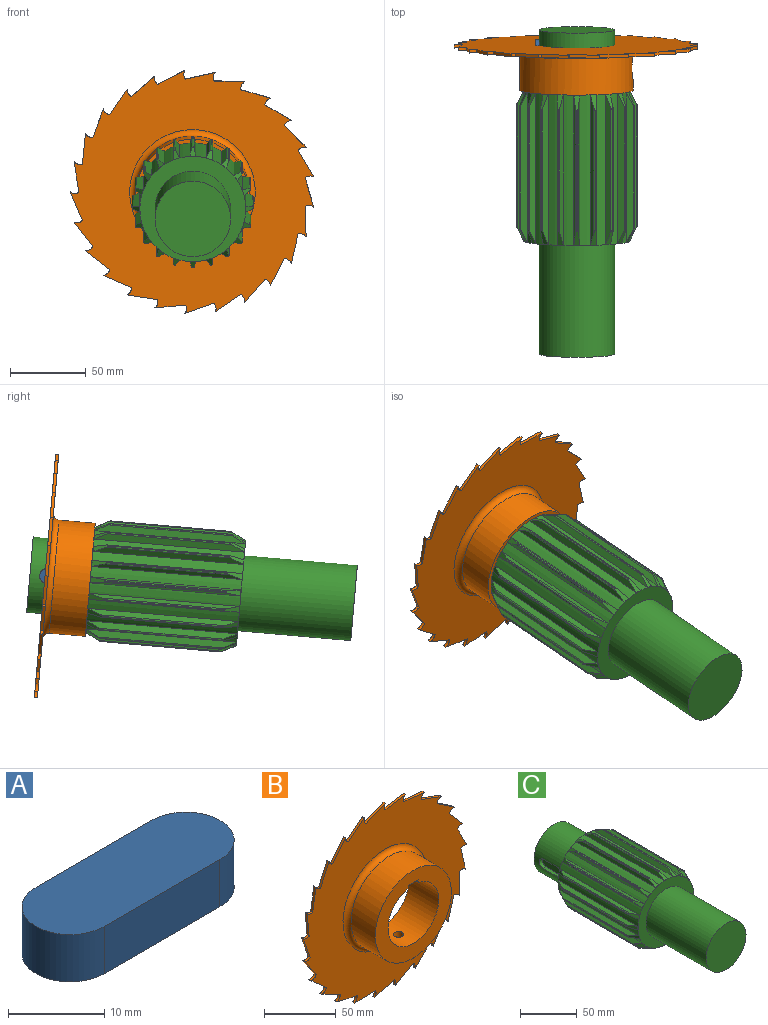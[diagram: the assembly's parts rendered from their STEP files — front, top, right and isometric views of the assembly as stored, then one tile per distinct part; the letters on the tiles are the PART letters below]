
ASSEMBLY  parts=3 mates=2
PART A: 6 faces, bbox 27x10x6 mm
  f0: plane 17x6mm, normal (0,1,0), area 102mm2, adj f1,f3,f4,f5
  f1: cylinder r=5mm len=10mm, axis (0,0,-1), area 94.2mm2, adj f0,f2,f4,f5
  f2: plane 17x6mm, normal (0,-1,0), area 102mm2, adj f1,f3,f4,f5
  f3: cylinder r=5mm len=10mm, axis (0,0,-1), area 94.2mm2, adj f0,f2,f4,f5
  f4: plane 27x10mm, normal (0,0,1), area 248.5mm2, adj f0,f1,f2,f3
  f5: plane 27x10mm, normal (0,0,-1), area 248.5mm2, adj f0,f1,f2,f3
PART B: 62 faces, bbox 161.2x30x160.9 mm
  f0: cylinder r=25mm len=50mm, axis (0,1,0), area 4371.8mm2, adj f6,f55,f56,f58,f61
  f1: cylinder r=37.5mm len=75mm, axis (0,1,0), area 5418.1mm2, adj f2,f58,f60
  f2: torus R=41.5mm, axis (0,-1,0), area 1537.7mm2, adj f1,f5,f59,f60
  f3: cylinder r=5mm len=4.13mm, axis (0,1,0), area 12.1mm2, adj f4,f5,f6,f54
  f4: plane 19.15x6.92mm, normal (0.34,0,0.94), area 40.7mm2, adj f3,f5,f6,f7
  f5: plane 161.18x160.86mm, normal (0,-1,0), area 13341.1mm2, adj f2,f3,f4,f7,f8,f9,f10,f11
  f6: plane 161.18x160.86mm, normal (0,1,0), area 16766.6mm2, adj f0,f3,f4,f7,f8,f9,f10,f11
  f7: cylinder r=5mm len=4.98mm, axis (0,1,0), area 12.1mm2, adj f4,f5,f6,f8
  f8: plane 20.27x2mm, normal (0.1,0,1), area 40.7mm2, adj f5,f6,f7,f9
  f9: cylinder r=5mm len=5.51mm, axis (0,1,0), area 12.1mm2, adj f5,f6,f8,f10
  f10: plane 20.12x3.16mm, normal (-0.16,0,0.99), area 40.7mm2, adj f5,f6,f9,f11
  f11: cylinder r=5mm len=5.7mm, axis (0,1,0), area 12.1mm2, adj f5,f6,f10,f12
  f12: plane 18.7x8.07mm, normal (-0.4,0,0.92), area 40.7mm2, adj f5,f6,f11,f13
  f13: cylinder r=5mm len=5.53mm, axis (0,1,0), area 12.1mm2, adj f5,f6,f12,f14
  f14: plane 16.1x12.46mm, normal (-0.61,0,0.79), area 40.7mm2, adj f5,f6,f13,f15
  f15: cylinder r=5mm len=5.01mm, axis (0,1,0), area 12.1mm2, adj f5,f6,f14,f16
  f16: plane 16.08x12.5mm, normal (-0.79,0,0.61), area 40.7mm2, adj f5,f6,f15,f17
  f17: cylinder r=5mm len=4.18mm, axis (0,1,0), area 12.1mm2, adj f5,f6,f16,f18
  f18: plane 18.68x8.11mm, normal (-0.92,0,0.4), area 40.7mm2, adj f5,f6,f17,f19
  f19: cylinder r=5mm len=4.79mm, axis (0,1,0), area 12.1mm2, adj f5,f6,f18,f20
  f20: plane 20.11x3.21mm, normal (-0.99,0,0.16), area 40.7mm2, adj f5,f6,f19,f21
  f21: cylinder r=5mm len=5.41mm, axis (0,1,0), area 12.1mm2, adj f5,f6,f20,f22
  f22: plane 20.28x2mm, normal (-1,0,-0.09), area 40.7mm2, adj f5,f6,f21,f23
  f23: cylinder r=5mm len=5.69mm, axis (0,1,0), area 12.1mm2, adj f5,f6,f22,f24
  f24: plane 19.17x6.88mm, normal (-0.94,0,-0.34), area 40.7mm2, adj f5,f6,f23,f25
  f25: cylinder r=5mm len=5.61mm, axis (0,1,0), area 12.1mm2, adj f5,f6,f24,f26
  f26: plane 16.86x11.43mm, normal (-0.83,0,-0.56), area 40.7mm2, adj f5,f6,f25,f27
  f27: cylinder r=5mm len=5.17mm, axis (0,1,0), area 12.1mm2, adj f5,f6,f26,f28
  f28: plane 15.26x13.48mm, normal (-0.66,0,-0.75), area 40.7mm2, adj f5,f6,f27,f29
  f29: cylinder r=5mm len=4.41mm, axis (0,1,0), area 12.1mm2, adj f5,f6,f28,f30
  f30: plane 18.13x9.27mm, normal (-0.45,0,-0.89), area 40.7mm2, adj f5,f6,f29,f31
  f31: cylinder r=5mm len=4.59mm, axis (0,1,0), area 12.1mm2, adj f5,f6,f30,f32
  f32: plane 19.87x4.46mm, normal (-0.22,0,-0.98), area 40.7mm2, adj f5,f6,f31,f33
  f33: cylinder r=5mm len=5.29mm, axis (0,1,0), area 12.1mm2, adj f5,f6,f32,f34
  f34: plane 20.35x2mm, normal (0.03,0,-1), area 40.7mm2, adj f5,f6,f33,f35
  f35: cylinder r=5mm len=5.65mm, axis (0,1,0), area 12.1mm2, adj f5,f6,f34,f36
  f36: plane 19.56x5.66mm, normal (0.28,0,-0.96), area 40.7mm2, adj f5,f6,f35,f37
  f37: cylinder r=5mm len=5.66mm, axis (0,1,0), area 12.1mm2, adj f5,f6,f36,f38
  f38: plane 17.54x10.35mm, normal (0.51,0,-0.86), area 40.7mm2, adj f5,f6,f37,f39
  f39: cylinder r=5mm len=5.31mm, axis (0,1,0), area 12.1mm2, adj f5,f6,f38,f40
  f40: plane 14.42x14.38mm, normal (0.71,0,-0.71), area 40.7mm2, adj f5,f6,f39,f41
  f41: cylinder r=5mm len=4.63mm, axis (0,1,0), area 12.1mm2, adj f5,f6,f40,f42
  f42: plane 17.52x10.39mm, normal (0.86,0,-0.51), area 40.7mm2, adj f5,f6,f41,f43
  f43: cylinder r=5mm len=4.37mm, axis (0,1,0), area 12.1mm2, adj f5,f6,f42,f44
  f44: plane 19.55x5.7mm, normal (0.96,0,-0.28), area 40.7mm2, adj f5,f6,f43,f45
  f45: cylinder r=5mm len=5.14mm, axis (0,1,0), area 12.1mm2, adj f5,f6,f44,f46
  f46: plane 20.35x2mm, normal (1,0,-0.03), area 40.7mm2, adj f5,f6,f45,f47
  f47: cylinder r=5mm len=5.59mm, axis (0,1,0), area 12.1mm2, adj f5,f6,f46,f48
  f48: plane 19.88x4.42mm, normal (0.98,0,0.22), area 40.7mm2, adj f5,f6,f47,f49
  f49: cylinder r=5mm len=5.69mm, axis (0,1,0), area 12.1mm2, adj f5,f6,f48,f50
  f50: plane 18.15x9.22mm, normal (0.89,0,0.45), area 40.7mm2, adj f5,f6,f49,f51
  f51: cylinder r=5mm len=5.43mm, axis (0,1,0), area 12.1mm2, adj f5,f6,f50,f52
  f52: plane 15.29x13.45mm, normal (0.75,0,0.66), area 40.7mm2, adj f5,f6,f51,f53
  f53: cylinder r=5mm len=4.83mm, axis (0,1,0), area 12.1mm2, adj f5,f6,f52,f54
  f54: plane 16.83x11.47mm, normal (0.56,0,0.83), area 40.7mm2, adj f3,f5,f6,f53
  f55: plane 30x2.51mm, normal (-1,0,0), area 75.2mm2, adj f0,f6,f57,f58
  f56: plane 30x2.51mm, normal (1,0,0), area 75.2mm2, adj f0,f6,f57,f58
  f57: plane 30x10mm, normal (0,0,-1), area 300mm2, adj f6,f55,f56,f58
  f58: plane 75x75mm, normal (0,-1,0), area 2432.7mm2, adj f0,f1,f55,f56,f57
  f59: plane 0.72x0.13mm, normal (0,0,1), area 0mm2, adj f2,f60
  f60: cone r=3.5mm half-angle=45deg, axis (0,0,-1), area 278.3mm2, adj f1,f2,f59,f61
  f61: cylinder r=3.5mm len=7.12mm, axis (0,0,-1), area 153.9mm2, adj f0,f60
PART C: 194 faces, bbox 80.1x215.1x80.1 mm
  f0: cylinder r=25mm len=50mm, axis (0,1,0), area 5994.6mm2, adj f1,f4,f187,f188,f189,f190,f192
  f1: plane 50x50mm, normal (0,1,0), area 1963.5mm2, adj f0
  f2: cylinder r=35mm len=100mm, axis (0,1,0), area 14010.6mm2, adj f3,f4,f5,f6,f8,f9,f14,f15
  f3: plane 70x70mm, normal (0,-1,0), area 1885mm2, adj f2,f185
  f4: plane 70x70mm, normal (0,1,0), area 1885mm2, adj f0,f2
  f5: plane 99.85x4.49mm, normal (0.97,0,0.24), area 420.8mm2, adj f2,f8,f9,f12
  f6: plane 99.85x4.49mm, normal (-0.97,0,0.24), area 420.8mm2, adj f2,f8,f9,f11
  f7: plane 79.64x0.33mm, normal (0,0,1), area 25.9mm2, adj f10,f11,f12,f13
  f8: plane 9.77x4.98mm, normal (0,-0.45,0.89), area 29.9mm2, adj f2,f5,f6,f11,f12,f13
  f9: plane 9.77x4.98mm, normal (0,0.45,0.89), area 29.9mm2, adj f2,f5,f6,f10,f11,f12
  f10: cylinder r=0.75mm len=1.01mm, axis (1,0,0), area 0.2mm2, adj f7,f9,f11,f12
  f11: cylinder r=0.75mm len=82.24mm, axis (0,1,0), area 80.5mm2, adj f6,f7,f8,f9,f10,f13
  f12: cylinder r=0.75mm len=82.24mm, axis (0,1,0), area 80.5mm2, adj f5,f7,f8,f9,f10,f13
  f13: cylinder r=0.75mm len=1.01mm, axis (1,0,0), area 0.2mm2, adj f7,f8,f11,f12
  f14: plane 99.85x3.93mm, normal (0.85,0,0.53), area 420.8mm2, adj f2,f17,f18,f21
  f15: plane 99.85x4.61mm, normal (-1,0,-0.07), area 420.8mm2, adj f2,f17,f18,f20
  f16: plane 79.64x0.31mm, normal (-0.31,0,0.95), area 25.9mm2, adj f19,f20,f21,f22
  f17: plane 9.77x5.51mm, normal (-0.28,-0.45,0.85), area 29.9mm2, adj f2,f14,f15,f20,f21,f22
  f18: plane 9.77x5.51mm, normal (-0.28,0.45,0.85), area 29.9mm2, adj f2,f14,f15,f19,f20,f21
  f19: cylinder r=0.75mm len=0.98mm, axis (0.95,0,0.31), area 0.2mm2, adj f16,f18,f20,f21
  f20: cylinder r=0.75mm len=82.24mm, axis (0,1,0), area 80.5mm2, adj f15,f16,f17,f18,f19,f22
  f21: cylinder r=0.75mm len=82.24mm, axis (0,1,0), area 80.5mm2, adj f14,f16,f17,f18,f19,f22
  f22: cylinder r=0.75mm len=0.98mm, axis (0.95,0,0.31), area 0.2mm2, adj f16,f17,f20,f21
  f23: plane 99.85x3.53mm, normal (0.64,0,0.76), area 420.8mm2, adj f2,f26,f27,f30
  f24: plane 99.85x4.28mm, normal (-0.93,0,-0.38), area 420.8mm2, adj f2,f26,f27,f29
  f25: plane 79.64x0.26mm, normal (-0.59,0,0.81), area 25.9mm2, adj f28,f29,f30,f31
  f26: plane 9.77x5.51mm, normal (-0.52,-0.45,0.72), area 29.9mm2, adj f2,f23,f24,f29,f30,f31
  f27: plane 9.77x5.51mm, normal (-0.52,0.45,0.72), area 29.9mm2, adj f2,f23,f24,f28,f29,f30
  f28: cylinder r=0.75mm len=0.86mm, axis (0.81,0,0.59), area 0.2mm2, adj f25,f27,f29,f30
  f29: cylinder r=0.75mm len=82.24mm, axis (0,1,0), area 80.5mm2, adj f24,f25,f26,f27,f28,f31
  f30: cylinder r=0.75mm len=82.24mm, axis (0,1,0), area 80.5mm2, adj f23,f25,f26,f27,f28,f31
  f31: cylinder r=0.75mm len=0.86mm, axis (0.81,0,0.59), area 0.2mm2, adj f25,f26,f29,f30
  f32: plane 99.85x4.28mm, normal (0.38,0,0.93), area 420.8mm2, adj f2,f35,f36,f39
  f33: plane 99.85x3.53mm, normal (-0.76,0,-0.64), area 420.8mm2, adj f2,f35,f36,f38
  f34: plane 79.64x0.26mm, normal (-0.81,0,0.59), area 25.9mm2, adj f37,f38,f39,f40
  f35: plane 9.77x5.51mm, normal (-0.72,-0.45,0.52), area 29.9mm2, adj f2,f32,f33,f38,f39,f40
  f36: plane 9.77x5.51mm, normal (-0.72,0.45,0.52), area 29.9mm2, adj f2,f32,f33,f37,f38,f39
  f37: cylinder r=0.75mm len=0.86mm, axis (0.59,0,0.81), area 0.2mm2, adj f34,f36,f38,f39
  f38: cylinder r=0.75mm len=82.24mm, axis (0,1,0), area 80.5mm2, adj f33,f34,f35,f36,f37,f40
  f39: cylinder r=0.75mm len=82.24mm, axis (0,1,0), area 80.5mm2, adj f32,f34,f35,f36,f37,f40
  f40: cylinder r=0.75mm len=0.86mm, axis (0.59,0,0.81), area 0.2mm2, adj f34,f35,f38,f39
  f41: plane 99.85x4.61mm, normal (0.07,0,1), area 420.8mm2, adj f2,f44,f45,f48
  f42: plane 99.85x3.93mm, normal (-0.53,0,-0.85), area 420.8mm2, adj f2,f44,f45,f47
  f43: plane 79.64x0.31mm, normal (-0.95,0,0.31), area 25.9mm2, adj f46,f47,f48,f49
  f44: plane 9.77x5.51mm, normal (-0.85,-0.45,0.28), area 29.9mm2, adj f2,f41,f42,f47,f48,f49
  f45: plane 9.77x5.51mm, normal (-0.85,0.45,0.28), area 29.9mm2, adj f2,f41,f42,f46,f47,f48
  f46: cylinder r=0.75mm len=0.98mm, axis (0.31,0,0.95), area 0.2mm2, adj f43,f45,f47,f48
  f47: cylinder r=0.75mm len=82.24mm, axis (0,1,0), area 80.5mm2, adj f42,f43,f44,f45,f46,f49
  f48: cylinder r=0.75mm len=82.24mm, axis (0,1,0), area 80.5mm2, adj f41,f43,f44,f45,f46,f49
  f49: cylinder r=0.75mm len=0.98mm, axis (0.31,0,0.95), area 0.2mm2, adj f43,f44,f47,f48
  f50: plane 99.85x4.49mm, normal (-0.24,0,0.97), area 420.8mm2, adj f2,f53,f54,f57
  f51: plane 99.85x4.49mm, normal (-0.24,0,-0.97), area 420.8mm2, adj f2,f53,f54,f56
  f52: plane 79.64x0.33mm, normal (-1,0,0), area 25.9mm2, adj f55,f56,f57,f58
  f53: plane 9.77x4.98mm, normal (-0.89,-0.45,0), area 29.9mm2, adj f2,f50,f51,f56,f57,f58
  f54: plane 9.77x4.98mm, normal (-0.89,0.45,0), area 29.9mm2, adj f2,f50,f51,f55,f56,f57
  f55: cylinder r=0.75mm len=1.01mm, axis (0,0,1), area 0.2mm2, adj f52,f54,f56,f57
  f56: cylinder r=0.75mm len=82.24mm, axis (0,1,0), area 80.5mm2, adj f51,f52,f53,f54,f55,f58
  f57: cylinder r=0.75mm len=82.24mm, axis (0,1,0), area 80.5mm2, adj f50,f52,f53,f54,f55,f58
  f58: cylinder r=0.75mm len=1.01mm, axis (0,0,1), area 0.2mm2, adj f52,f53,f56,f57
  f59: plane 99.85x3.93mm, normal (-0.53,0,0.85), area 420.8mm2, adj f2,f62,f63,f66
  f60: plane 99.85x4.61mm, normal (0.07,0,-1), area 420.8mm2, adj f2,f62,f63,f65
  f61: plane 79.64x0.31mm, normal (-0.95,0,-0.31), area 25.9mm2, adj f64,f65,f66,f67
  f62: plane 9.77x5.51mm, normal (-0.85,-0.45,-0.28), area 29.9mm2, adj f2,f59,f60,f65,f66,f67
  f63: plane 9.77x5.51mm, normal (-0.85,0.45,-0.28), area 29.9mm2, adj f2,f59,f60,f64,f65,f66
  f64: cylinder r=0.75mm len=0.98mm, axis (-0.31,0,0.95), area 0.2mm2, adj f61,f63,f65,f66
  f65: cylinder r=0.75mm len=82.24mm, axis (0,1,0), area 80.5mm2, adj f60,f61,f62,f63,f64,f67
  f66: cylinder r=0.75mm len=82.24mm, axis (0,1,0), area 80.5mm2, adj f59,f61,f62,f63,f64,f67
  f67: cylinder r=0.75mm len=0.98mm, axis (-0.31,0,0.95), area 0.2mm2, adj f61,f62,f65,f66
  f68: plane 99.85x3.53mm, normal (-0.76,0,0.64), area 420.8mm2, adj f2,f71,f72,f75
  f69: plane 99.85x4.28mm, normal (0.38,0,-0.93), area 420.8mm2, adj f2,f71,f72,f74
  f70: plane 79.64x0.26mm, normal (-0.81,0,-0.59), area 25.9mm2, adj f73,f74,f75,f76
  f71: plane 9.77x5.51mm, normal (-0.72,-0.45,-0.52), area 29.9mm2, adj f2,f68,f69,f74,f75,f76
  f72: plane 9.77x5.51mm, normal (-0.72,0.45,-0.52), area 29.9mm2, adj f2,f68,f69,f73,f74,f75
  f73: cylinder r=0.75mm len=0.86mm, axis (-0.59,0,0.81), area 0.2mm2, adj f70,f72,f74,f75
  f74: cylinder r=0.75mm len=82.24mm, axis (0,1,0), area 80.5mm2, adj f69,f70,f71,f72,f73,f76
  f75: cylinder r=0.75mm len=82.24mm, axis (0,1,0), area 80.5mm2, adj f68,f70,f71,f72,f73,f76
  f76: cylinder r=0.75mm len=0.86mm, axis (-0.59,0,0.81), area 0.2mm2, adj f70,f71,f74,f75
  f77: plane 99.85x4.28mm, normal (-0.93,0,0.38), area 420.8mm2, adj f2,f80,f81,f84
  f78: plane 99.85x3.53mm, normal (0.64,0,-0.76), area 420.8mm2, adj f2,f80,f81,f83
  f79: plane 79.64x0.26mm, normal (-0.59,0,-0.81), area 25.9mm2, adj f82,f83,f84,f85
  f80: plane 9.77x5.51mm, normal (-0.52,-0.45,-0.72), area 29.9mm2, adj f2,f77,f78,f83,f84,f85
  f81: plane 9.77x5.51mm, normal (-0.52,0.45,-0.72), area 29.9mm2, adj f2,f77,f78,f82,f83,f84
  f82: cylinder r=0.75mm len=0.86mm, axis (-0.81,0,0.59), area 0.2mm2, adj f79,f81,f83,f84
  f83: cylinder r=0.75mm len=82.24mm, axis (0,1,0), area 80.5mm2, adj f78,f79,f80,f81,f82,f85
  f84: cylinder r=0.75mm len=82.24mm, axis (0,1,0), area 80.5mm2, adj f77,f79,f80,f81,f82,f85
  f85: cylinder r=0.75mm len=0.86mm, axis (-0.81,0,0.59), area 0.2mm2, adj f79,f80,f83,f84
  f86: plane 99.85x4.61mm, normal (-1,0,0.07), area 420.8mm2, adj f2,f89,f90,f93
  f87: plane 99.85x3.93mm, normal (0.85,0,-0.53), area 420.8mm2, adj f2,f89,f90,f92
  f88: plane 79.64x0.31mm, normal (-0.31,0,-0.95), area 25.9mm2, adj f91,f92,f93,f94
  f89: plane 9.77x5.51mm, normal (-0.28,-0.45,-0.85), area 29.9mm2, adj f2,f86,f87,f92,f93,f94
  f90: plane 9.77x5.51mm, normal (-0.28,0.45,-0.85), area 29.9mm2, adj f2,f86,f87,f91,f92,f93
  f91: cylinder r=0.75mm len=0.98mm, axis (-0.95,0,0.31), area 0.2mm2, adj f88,f90,f92,f93
  f92: cylinder r=0.75mm len=82.24mm, axis (0,1,0), area 80.5mm2, adj f87,f88,f89,f90,f91,f94
  f93: cylinder r=0.75mm len=82.24mm, axis (0,1,0), area 80.5mm2, adj f86,f88,f89,f90,f91,f94
  f94: cylinder r=0.75mm len=0.98mm, axis (-0.95,0,0.31), area 0.2mm2, adj f88,f89,f92,f93
  f95: plane 99.85x4.49mm, normal (-0.97,0,-0.24), area 420.8mm2, adj f2,f98,f99,f102
  f96: plane 99.85x4.49mm, normal (0.97,0,-0.24), area 420.8mm2, adj f2,f98,f99,f101
  f97: plane 79.64x0.33mm, normal (0,0,-1), area 25.9mm2, adj f100,f101,f102,f103
  f98: plane 9.82x5.03mm, normal (0,-0.45,-0.89), area 29.9mm2, adj f2,f95,f96,f101,f102,f103
  f99: plane 9.82x5.03mm, normal (0,0.45,-0.89), area 29.9mm2, adj f2,f95,f96,f100,f101,f102
  f100: cylinder r=0.75mm len=1.01mm, axis (-1,0,0), area 0.2mm2, adj f97,f99,f101,f102
  f101: cylinder r=0.75mm len=82.24mm, axis (0,1,0), area 80.5mm2, adj f96,f97,f98,f99,f100,f103
  f102: cylinder r=0.75mm len=82.24mm, axis (0,1,0), area 80.5mm2, adj f95,f97,f98,f99,f100,f103
  f103: cylinder r=0.75mm len=1.01mm, axis (-1,0,0), area 0.2mm2, adj f97,f98,f101,f102
  f104: plane 99.85x3.93mm, normal (-0.85,0,-0.53), area 420.8mm2, adj f2,f107,f108,f111
  f105: plane 99.85x4.61mm, normal (1,0,0.07), area 420.8mm2, adj f2,f107,f108,f110
  f106: plane 79.64x0.31mm, normal (0.31,0,-0.95), area 25.9mm2, adj f109,f110,f111,f112
  f107: plane 9.77x5.51mm, normal (0.28,-0.45,-0.85), area 29.9mm2, adj f2,f104,f105,f110,f111,f112
  f108: plane 9.77x5.51mm, normal (0.28,0.45,-0.85), area 29.9mm2, adj f2,f104,f105,f109,f110,f111
  f109: cylinder r=0.75mm len=0.98mm, axis (-0.95,0,-0.31), area 0.2mm2, adj f106,f108,f110,f111
  f110: cylinder r=0.75mm len=82.24mm, axis (0,1,0), area 80.5mm2, adj f105,f106,f107,f108,f109,f112
  f111: cylinder r=0.75mm len=82.24mm, axis (0,1,0), area 80.5mm2, adj f104,f106,f107,f108,f109,f112
  f112: cylinder r=0.75mm len=0.98mm, axis (-0.95,0,-0.31), area 0.2mm2, adj f106,f107,f110,f111
  f113: plane 99.85x3.53mm, normal (-0.64,0,-0.76), area 420.8mm2, adj f2,f116,f117,f120
  f114: plane 99.85x4.28mm, normal (0.93,0,0.38), area 420.8mm2, adj f2,f116,f117,f119
  f115: plane 79.64x0.26mm, normal (0.59,0,-0.81), area 25.9mm2, adj f118,f119,f120,f121
  f116: plane 9.77x5.51mm, normal (0.52,-0.45,-0.72), area 29.9mm2, adj f2,f113,f114,f119,f120,f121
  f117: plane 9.77x5.51mm, normal (0.52,0.45,-0.72), area 29.9mm2, adj f2,f113,f114,f118,f119,f120
  f118: cylinder r=0.75mm len=0.86mm, axis (-0.81,0,-0.59), area 0.2mm2, adj f115,f117,f119,f120
  f119: cylinder r=0.75mm len=82.24mm, axis (0,1,0), area 80.5mm2, adj f114,f115,f116,f117,f118,f121
  f120: cylinder r=0.75mm len=82.24mm, axis (0,1,0), area 80.5mm2, adj f113,f115,f116,f117,f118,f121
  f121: cylinder r=0.75mm len=0.86mm, axis (-0.81,0,-0.59), area 0.2mm2, adj f115,f116,f119,f120
  f122: plane 99.85x4.28mm, normal (-0.38,0,-0.93), area 420.8mm2, adj f2,f125,f126,f129
  f123: plane 99.85x3.53mm, normal (0.76,0,0.64), area 420.8mm2, adj f2,f125,f126,f128
  f124: plane 79.64x0.26mm, normal (0.81,0,-0.59), area 25.9mm2, adj f127,f128,f129,f130
  f125: plane 9.77x5.51mm, normal (0.72,-0.45,-0.52), area 29.9mm2, adj f2,f122,f123,f128,f129,f130
  f126: plane 9.77x5.51mm, normal (0.72,0.45,-0.52), area 29.9mm2, adj f2,f122,f123,f127,f128,f129
  f127: cylinder r=0.75mm len=0.86mm, axis (-0.59,0,-0.81), area 0.2mm2, adj f124,f126,f128,f129
  f128: cylinder r=0.75mm len=82.24mm, axis (0,1,0), area 80.5mm2, adj f123,f124,f125,f126,f127,f130
  f129: cylinder r=0.75mm len=82.24mm, axis (0,1,0), area 80.5mm2, adj f122,f124,f125,f126,f127,f130
  f130: cylinder r=0.75mm len=0.86mm, axis (-0.59,0,-0.81), area 0.2mm2, adj f124,f125,f128,f129
  f131: plane 99.85x4.61mm, normal (-0.07,0,-1), area 420.8mm2, adj f2,f134,f135,f138
  f132: plane 99.85x3.93mm, normal (0.53,0,0.85), area 420.8mm2, adj f2,f134,f135,f137
  f133: plane 79.64x0.31mm, normal (0.95,0,-0.31), area 25.9mm2, adj f136,f137,f138,f139
  f134: plane 9.77x5.51mm, normal (0.85,-0.45,-0.28), area 29.9mm2, adj f2,f131,f132,f137,f138,f139
  f135: plane 9.77x5.51mm, normal (0.85,0.45,-0.28), area 29.9mm2, adj f2,f131,f132,f136,f137,f138
  f136: cylinder r=0.75mm len=0.98mm, axis (-0.31,0,-0.95), area 0.2mm2, adj f133,f135,f137,f138
  f137: cylinder r=0.75mm len=82.24mm, axis (0,1,0), area 80.5mm2, adj f132,f133,f134,f135,f136,f139
  f138: cylinder r=0.75mm len=82.24mm, axis (0,1,0), area 80.5mm2, adj f131,f133,f134,f135,f136,f139
  f139: cylinder r=0.75mm len=0.98mm, axis (-0.31,0,-0.95), area 0.2mm2, adj f133,f134,f137,f138
  f140: plane 99.85x4.49mm, normal (0.24,0,-0.97), area 420.8mm2, adj f2,f143,f144,f147
  f141: plane 99.85x4.49mm, normal (0.24,0,0.97), area 420.8mm2, adj f2,f143,f144,f146
  f142: plane 79.64x0.33mm, normal (1,0,0), area 25.9mm2, adj f145,f146,f147,f148
  f143: plane 9.77x4.98mm, normal (0.89,-0.45,0), area 29.9mm2, adj f2,f140,f141,f146,f147,f148
  f144: plane 9.77x4.98mm, normal (0.89,0.45,0), area 29.9mm2, adj f2,f140,f141,f145,f146,f147
  f145: cylinder r=0.75mm len=1.01mm, axis (0,0,-1), area 0.2mm2, adj f142,f144,f146,f147
  f146: cylinder r=0.75mm len=82.24mm, axis (0,1,0), area 80.5mm2, adj f141,f142,f143,f144,f145,f148
  f147: cylinder r=0.75mm len=82.24mm, axis (0,1,0), area 80.5mm2, adj f140,f142,f143,f144,f145,f148
  f148: cylinder r=0.75mm len=1.01mm, axis (0,0,-1), area 0.2mm2, adj f142,f143,f146,f147
  f149: plane 99.85x3.93mm, normal (0.53,0,-0.85), area 420.8mm2, adj f2,f152,f153,f156
  f150: plane 99.85x4.61mm, normal (-0.07,0,1), area 420.8mm2, adj f2,f152,f153,f155
  f151: plane 79.64x0.31mm, normal (0.95,0,0.31), area 25.9mm2, adj f154,f155,f156,f157
  f152: plane 9.77x5.51mm, normal (0.85,-0.45,0.28), area 29.9mm2, adj f2,f149,f150,f155,f156,f157
  f153: plane 9.77x5.51mm, normal (0.85,0.45,0.28), area 29.9mm2, adj f2,f149,f150,f154,f155,f156
  f154: cylinder r=0.75mm len=0.98mm, axis (0.31,0,-0.95), area 0.2mm2, adj f151,f153,f155,f156
  f155: cylinder r=0.75mm len=82.24mm, axis (0,1,0), area 80.5mm2, adj f150,f151,f152,f153,f154,f157
  f156: cylinder r=0.75mm len=82.24mm, axis (0,1,0), area 80.5mm2, adj f149,f151,f152,f153,f154,f157
  f157: cylinder r=0.75mm len=0.98mm, axis (0.31,0,-0.95), area 0.2mm2, adj f151,f152,f155,f156
  f158: plane 99.85x3.53mm, normal (0.76,0,-0.64), area 420.8mm2, adj f2,f161,f162,f165
  f159: plane 99.85x4.28mm, normal (-0.38,0,0.93), area 420.8mm2, adj f2,f161,f162,f164
  f160: plane 79.64x0.26mm, normal (0.81,0,0.59), area 25.9mm2, adj f163,f164,f165,f166
  f161: plane 9.77x5.51mm, normal (0.72,-0.45,0.52), area 29.9mm2, adj f2,f158,f159,f164,f165,f166
  f162: plane 9.77x5.51mm, normal (0.72,0.45,0.52), area 29.9mm2, adj f2,f158,f159,f163,f164,f165
  f163: cylinder r=0.75mm len=0.86mm, axis (0.59,0,-0.81), area 0.2mm2, adj f160,f162,f164,f165
  f164: cylinder r=0.75mm len=82.24mm, axis (0,1,0), area 80.5mm2, adj f159,f160,f161,f162,f163,f166
  f165: cylinder r=0.75mm len=82.24mm, axis (0,1,0), area 80.5mm2, adj f158,f160,f161,f162,f163,f166
  f166: cylinder r=0.75mm len=0.86mm, axis (0.59,0,-0.81), area 0.2mm2, adj f160,f161,f164,f165
  f167: plane 99.85x4.28mm, normal (0.93,0,-0.38), area 420.8mm2, adj f2,f170,f171,f174
  f168: plane 99.85x3.53mm, normal (-0.64,0,0.76), area 420.8mm2, adj f2,f170,f171,f173
  f169: plane 79.64x0.26mm, normal (0.59,0,0.81), area 25.9mm2, adj f172,f173,f174,f175
  f170: plane 9.77x5.51mm, normal (0.52,-0.45,0.72), area 29.9mm2, adj f2,f167,f168,f173,f174,f175
  f171: plane 9.77x5.51mm, normal (0.52,0.45,0.72), area 29.9mm2, adj f2,f167,f168,f172,f173,f174
  f172: cylinder r=0.75mm len=0.86mm, axis (0.81,0,-0.59), area 0.2mm2, adj f169,f171,f173,f174
  f173: cylinder r=0.75mm len=82.24mm, axis (0,1,0), area 80.5mm2, adj f168,f169,f170,f171,f172,f175
  f174: cylinder r=0.75mm len=82.24mm, axis (0,1,0), area 80.5mm2, adj f167,f169,f170,f171,f172,f175
  f175: cylinder r=0.75mm len=0.86mm, axis (0.81,0,-0.59), area 0.2mm2, adj f169,f170,f173,f174
  f176: plane 99.85x4.61mm, normal (1,0,-0.07), area 420.8mm2, adj f2,f179,f180,f183
  f177: plane 99.85x3.93mm, normal (-0.85,0,0.53), area 420.8mm2, adj f2,f179,f180,f182
  f178: plane 79.64x0.31mm, normal (0.31,0,0.95), area 25.9mm2, adj f181,f182,f183,f184
  f179: plane 9.77x5.51mm, normal (0.28,-0.45,0.85), area 29.9mm2, adj f2,f176,f177,f182,f183,f184
  f180: plane 9.77x5.51mm, normal (0.28,0.45,0.85), area 29.9mm2, adj f2,f176,f177,f181,f182,f183
  f181: cylinder r=0.75mm len=0.98mm, axis (0.95,0,-0.31), area 0.2mm2, adj f178,f180,f182,f183
  f182: cylinder r=0.75mm len=82.24mm, axis (0,1,0), area 80.5mm2, adj f177,f178,f179,f180,f181,f184
  f183: cylinder r=0.75mm len=82.24mm, axis (0,1,0), area 80.5mm2, adj f176,f178,f179,f180,f181,f184
  f184: cylinder r=0.75mm len=0.98mm, axis (0.95,0,-0.31), area 0.2mm2, adj f178,f179,f182,f183
  f185: cylinder r=25mm len=75mm, axis (0,1,0), area 11781mm2, adj f3,f186
  f186: plane 50x50mm, normal (0,-1,0), area 1963.5mm2, adj f185
  f187: plane 17x3.5mm, normal (0,0,-1), area 59.4mm2, adj f0,f188,f190,f191
  f188: cylinder r=5mm len=10mm, axis (-1,0,0), area 58.9mm2, adj f0,f187,f189,f191
  f189: plane 17x3.5mm, normal (0,0,1), area 59.4mm2, adj f0,f188,f190,f191
  f190: cylinder r=5mm len=10mm, axis (-1,0,0), area 58.9mm2, adj f0,f187,f189,f191
  f191: plane 27x10mm, normal (-1,0,0), area 248.5mm2, adj f187,f188,f189,f190
  f192: cylinder r=3.5mm len=10mm, axis (1,0,0), area 217.2mm2, adj f0,f193
  f193: cone r=0mm half-angle=59deg, axis (1,0,0), area 44.9mm2, adj f192
PLACE A rot(axis=(0.59,0.54,0.59),122.9deg) t=(-17.51,193.79,19.38)mm
PLACE B rot(axis=(0.04,-1,-0.04),90.1deg) t=(9.25,203.75,20.25)mm
PLACE C rot(axis=(1,0,0),5deg) t=(9.49,213.71,21.12)mm
MATE fastened C.f191 <-> A.f4  axis (-1,0,0) through (-11.51,193.79,19.38)mm
MATE fastened C.f185 <-> B.f58  axis (0,1,0.09) through (9.49,173.86,17.64)mm
